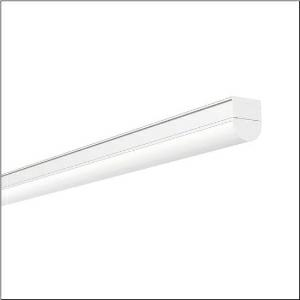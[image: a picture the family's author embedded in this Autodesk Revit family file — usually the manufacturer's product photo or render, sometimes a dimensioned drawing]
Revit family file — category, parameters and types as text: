
# Revit family: ecopack_r__31_51lj12dkm40a_26af
name_source: partatom
category: Lighting Fixtures
units: mm (PartAtom-declared; Revit-internal decimal feet)

## family parameters
Cut with Voids When Loaded = No
Host = Face
Light Source = No
Part Type = Normal
Room Calculation Point = No
Round Connector Dimension = Use Diameter
Shared = No

## types (1)
- --- (1 x LED, 4290 lm, 33 W, 5000K)
    Apparent Load = 33 VA
    CIE Flux Codes = 39 67 87 89 100
    Color Rendering = 80
    Color Temperature = 5000K
    Default Elevation = 1800 mm
    Description = Ecopack® 31, diffuser luminaire, primary optical cover: cover, of PC, frosted, light emission: direct distribution, primary light characteristic: symmetric, installation type: surface-mounted, LED, rated luminous flux: 4.300lm, luminous efficacy: 130lm/W, light colour: 830/840/850, colour temperature: 3000/4000/5000K, control gear: DALI 2, with terminal, 5-pole, mains connection: 220..240V, AC, 50/60Hz, rated input power: 33W, housing, of aluminium, traffic white (RAL 9016), length: 1.150mm, width: 56mm, height: 68mm, end cap, of PC, white, protection rating (complete): IP20, insulation class (complete): insulation class I (protective earthing), certification: CE, impact resistance: IK06, permissible operating ambient temperature: -20..+40°C, packaging unit: 1 piece
    Height = 68 mm
    Lamp = 1 x LED
    Lamp Light Flux = 4290 lm
    Lamp Power = 33 W
    Lamp count = 1
    Length = 1149 mm
    Luminous efficacy = 130 lm/W
    Manufacturer = Siteco
    ModVariant = No
    Model = 51LJ12DKM40A
    Mounting Place = Ceiling
    Mounting Type = Surface mounted
    Number of Poles = 1
    OnlyDefault = Yes
    Power Factor = 1
    Product Name = Ecopack® 31
    Product group = diffuser luminaire
    ProductGroupID = 306
    Protection Class = Protection class I
    Protection Degree = IP 20
    RLX_Detail_Level = 1
    RLX_Emergency_Light_Flux = 0 lm
    RLX_Emergency_Type = 0
    RLX_Emergency_Type_DB = No
    RlxData = <blob elided: 24921 chars, md5=75c9c6c8>
    Socket = socket
    Standby Power = 0 W
    System Light Flux = 4290 lm
    System Power = 33 W
    Type Comments = individual setting: colour temperature 5000K
    Type Image = l_1007030.jpg
    URL = http://relux.com
    VarID = @adj_174000
    Voltage = 0 V
    Weight = 0.00 kg
    Width = 56 mm

## geometry (parser evidence)
native form markers: Blend x4, Sweep x12
no freeform markers — native parametric forms only
